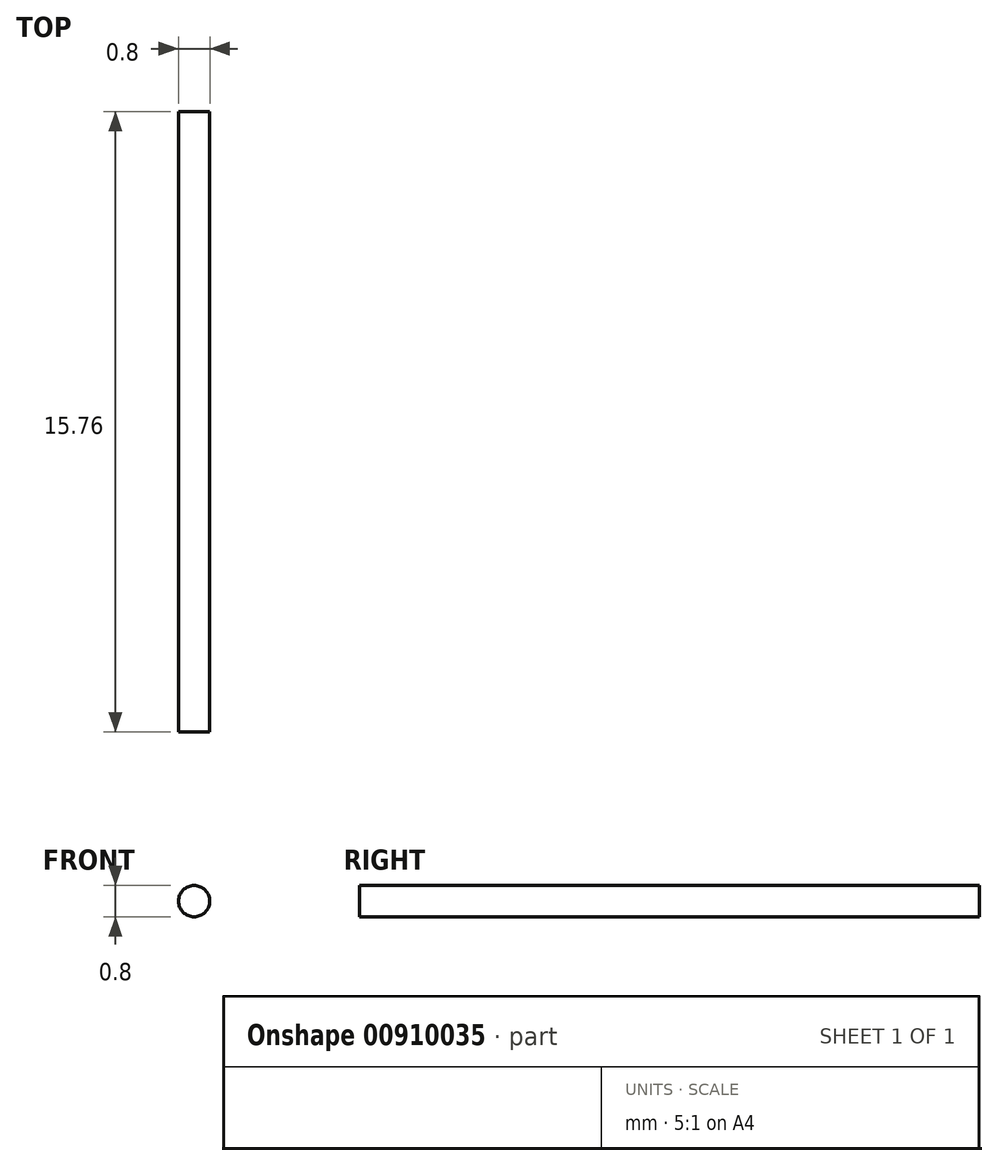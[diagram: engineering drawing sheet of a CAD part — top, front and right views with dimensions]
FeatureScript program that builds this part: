
annotation { "Feature Type Name" : "Feature", "Feature Type Description" : "" }
export const myFeature = defineFeature(function(context is Context, id is Id, definition is map)
    precondition{}
    {
        {
            var Q0;
            Q0=qCreatedBy(makeId("Front.planeOp"),FACE);
            var sketch = newSketch(context, id + "F0", { "sketchPlane" : qUnion([Q0])});
            skCircle(sketch, "E0", {"center": v(0, 0) * mm, "radius": 0.4 * mm});
            skSolve(sketch);
        }
        {
            var Q0;
            Q0 = qSketchRegion(id + "F0", true);
            extrude(context, id + "F1", {"entities" : qUnion([Q0]), "endBound" : BoundingType.SYMMETRIC, "depth" : (15 + 2 * (3 / 8)) * mm, "offsetDistance" : 25.4 * mm});
        }
    });
